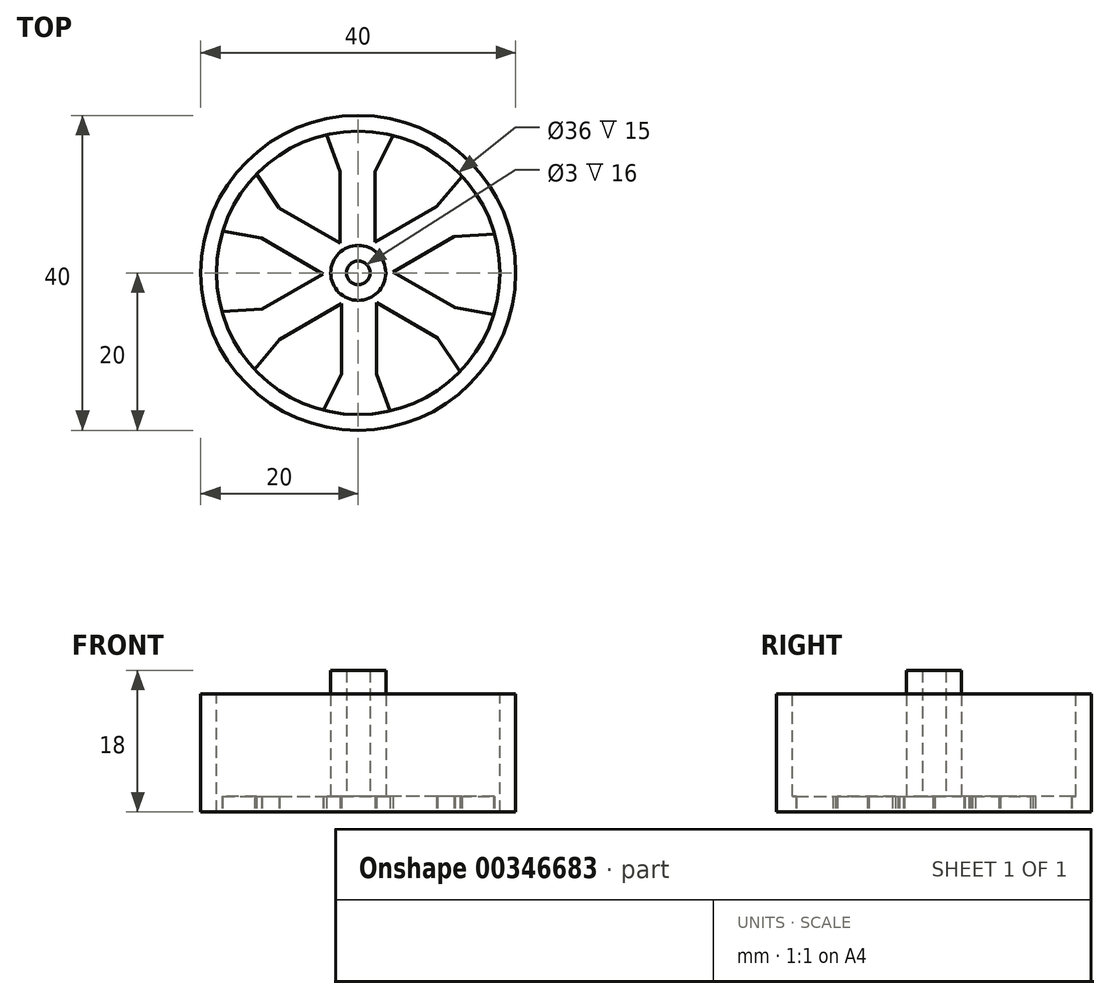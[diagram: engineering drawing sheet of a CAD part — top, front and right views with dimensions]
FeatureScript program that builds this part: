
annotation { "Feature Type Name" : "Feature", "Feature Type Description" : "" }
export const myFeature = defineFeature(function(context is Context, id is Id, definition is map)
    precondition{}
    {
        {
            var Q0;
            Q0=qCreatedBy(makeId("Top.planeOp"),FACE);
            var sketch = newSketch(context, id + "F0", { "sketchPlane" : qUnion([Q0])});
            skCircle(sketch, "E0", {"center": v(0, 0) * mm, "radius": 20 * mm});
            skSolve(sketch);
        }
        {
            var Q0;
            Q0=makeQuery(id+"F0.imprint","IMPRINT",FACE,{"disambiguationData":[TD([[makeQuery(id+"F0.imprint","IMPRINT",EDGE,{"derivedFrom":sQuery(id+"F0.wireOp",EDGE,"E0")}),1.0]])]});
            extrude(context, id + "F1", {"entities" : qUnion([Q0]), "depth" : 15 * mm});
        }
        {
            var Q0;
            Q0=makeQuery(id+"F1.opExtrude","CAP_FACE",FACE,{"disambiguationData":[OSD([sQuery(id+"F0.wireOp",EDGE,"E0")])],"isStart":false});
            var sketch = newSketch(context, id + "F2", { "sketchPlane" : qUnion([Q0])});
            skCircle(sketch, "E1", {"center": v(0, 0) * mm, "radius": 18 * mm});
            skSolve(sketch);
        }
        {
            var Q0;
            Q0=makeQuery(id+"F2.imprint","IMPRINT",FACE,{"disambiguationData":[TD([[makeQuery(id+"F2.imprint","IMPRINT",EDGE,{"derivedFrom":sQuery(id+"F2.wireOp",EDGE,"E1")}),1.0]])]});
            extrude(context, id + "F3", {"entities" : qUnion([Q0]), "operationType" : NewBodyOperationType.REMOVE, "oppositeDirection" : true, "depth" : 13 * mm});
        }
        {
            var Q0;
            Q0=makeQuery(id+"F3.boolean.opBoolean","COPY",FACE,{"derivedFrom":makeQuery(id+"F3.opExtrude","CAP_FACE",FACE,{"disambiguationData":[OSD([sQuery(id+"F2.wireOp",EDGE,"E1")])],"isStart":false})});
            var sketch = newSketch(context, id + "F4", { "sketchPlane" : qUnion([Q0])});
            skCircle(sketch, "E2", {"center": v(0, 0) * mm, "radius": 1.5 * mm});
            skCircle(sketch, "E3", {"center": v(0, 0) * mm, "radius": 3.5 * mm});
            skSolve(sketch);
        }
        {
            var Q0;
            Q0=makeQuery(id+"F4.imprint","IMPRINT",FACE,{"disambiguationData":[TD([[makeQuery(id+"F4.imprint","IMPRINT",EDGE,{"derivedFrom":sQuery(id+"F4.wireOp",EDGE,"E2")}),-1.0]])]});
            extrude(context, id + "F5", {"entities" : qUnion([Q0]), "operationType" : NewBodyOperationType.ADD, "depth" : 16 * mm});
        }
        {
            var Q0;
            Q0=qCreatedBy(makeId("Top.planeOp"),FACE);
            var sketch = newSketch(context, id + "F6", { "sketchPlane" : qUnion([Q0])});
            skCircle(sketch, "E4", {"center": v(0, 0) * mm, "radius": 18 * mm});
            skSolve(sketch);
        }
        {
            var Q0;
            Q0=makeQuery(id+"F6.imprint","IMPRINT",FACE,{"disambiguationData":[TD([[makeQuery(id+"F6.imprint","IMPRINT",EDGE,{"derivedFrom":sQuery(id+"F6.wireOp",EDGE,"E4")}),1.0]])]});
            var sketch = newSketch(context, id + "F7", { "sketchPlane" : qUnion([Q0])});
            skLineSegment(sketch, "E5", {"start": v(-2.12, -0.86) * mm, "end": v(-2.12, -12.86) * mm});
            skLineSegment(sketch, "E6", {"start": v(2.33, -0.86) * mm, "end": v(2.33, -12.86) * mm});
            skLineSegment(sketch, "E7", {"start": v(2.33, -12.86) * mm, "end": v(4.42, -18.61) * mm});
            skLineSegment(sketch, "E8", {"start": v(-2.12, -12.86) * mm, "end": v(-5, -18.61) * mm});
            skLineSegment(sketch, "E9.1.0", {"start": v(-0.32, -2.26) * mm, "end": v(10.08, -8.26) * mm});
            skLineSegment(sketch, "E9.1.1", {"start": v(10.08, -8.26) * mm, "end": v(13.62, -13.63) * mm});
            skLineSegment(sketch, "E9.1.2", {"start": v(12.3, -4.42) * mm, "end": v(18.33, -5.48) * mm});
            skLineSegment(sketch, "E9.1.3", {"start": v(1.9, 1.58) * mm, "end": v(12.3, -4.42) * mm});
            skLineSegment(sketch, "E9.2.0", {"start": v(1.8, -1.4) * mm, "end": v(12.2, 4.6) * mm});
            skLineSegment(sketch, "E9.2.1", {"start": v(12.2, 4.6) * mm, "end": v(18.61, 4.98) * mm});
            skLineSegment(sketch, "E9.2.2", {"start": v(9.97, 8.44) * mm, "end": v(13.9, 13.13) * mm});
            skLineSegment(sketch, "E9.2.3", {"start": v(-0.42, 2.44) * mm, "end": v(9.97, 8.44) * mm});
            skLineSegment(sketch, "E9.3.0", {"start": v(2.12, 0.86) * mm, "end": v(2.12, 12.86) * mm});
            skLineSegment(sketch, "E9.3.1", {"start": v(2.12, 12.86) * mm, "end": v(5, 18.61) * mm});
            skLineSegment(sketch, "E9.3.2", {"start": v(-2.33, 12.86) * mm, "end": v(-4.42, 18.61) * mm});
            skLineSegment(sketch, "E9.3.3", {"start": v(-2.33, 0.86) * mm, "end": v(-2.33, 12.86) * mm});
            skLineSegment(sketch, "E9.4.0", {"start": v(0.32, 2.26) * mm, "end": v(-10.08, 8.26) * mm});
            skLineSegment(sketch, "E9.4.1", {"start": v(-10.08, 8.26) * mm, "end": v(-13.62, 13.63) * mm});
            skLineSegment(sketch, "E9.4.2", {"start": v(-12.3, 4.42) * mm, "end": v(-18.33, 5.48) * mm});
            skLineSegment(sketch, "E9.4.3", {"start": v(-1.9, -1.58) * mm, "end": v(-12.3, 4.42) * mm});
            skLineSegment(sketch, "E9.5.0", {"start": v(-1.8, 1.4) * mm, "end": v(-12.2, -4.6) * mm});
            skLineSegment(sketch, "E9.5.1", {"start": v(-12.2, -4.6) * mm, "end": v(-18.61, -4.98) * mm});
            skLineSegment(sketch, "E9.5.2", {"start": v(-9.97, -8.44) * mm, "end": v(-13.9, -13.13) * mm});
            skLineSegment(sketch, "E9.5.3", {"start": v(0.42, -2.44) * mm, "end": v(-9.97, -8.44) * mm});
            skPoint(sketch, "E9.center", {"position": v(0, 0) * mm});
            skSolve(sketch);
        }
        {
            var Q0;
            {var subQ3=sQuery(id+"F7.wireOp",EDGE,"E6");var subQ5=sQuery(id+"F7.wireOp",EDGE,"E7");var subQ6=makeQuery(id+"F7.imprint","INTERSECT",VERTEX,{"derivedFrom":[subQ3,subQ5]});Q0=makeQuery(id+"F7.imprint","IMPRINT",FACE,{"disambiguationData":[TD([[makeQuery(id+"F7.imprint","IMPRINT",EDGE,{"disambiguationData":[TD([[subQ6,1.0]])],"derivedFrom":subQ3}),1.0]])]});}
            var Q1;
            {var subQ5=sQuery(id+"F7.wireOp",EDGE,"E5");var subQ7=sQuery(id+"F7.wireOp",EDGE,"E8");var subQ8=makeQuery(id+"F7.imprint","INTERSECT",VERTEX,{"derivedFrom":[subQ5,subQ7]});Q1=makeQuery(id+"F7.imprint","IMPRINT",FACE,{"disambiguationData":[TD([[makeQuery(id+"F7.imprint","IMPRINT",EDGE,{"disambiguationData":[TD([[subQ8,1.0]])],"derivedFrom":subQ5}),-1.0]])]});}
            var Q2;
            {var subQ3=sQuery(id+"F7.wireOp",EDGE,"E9.4.3");var subQ5=sQuery(id+"F7.wireOp",EDGE,"E9.4.2");var subQ6=makeQuery(id+"F7.imprint","INTERSECT",VERTEX,{"derivedFrom":[subQ5,subQ3]});Q2=makeQuery(id+"F7.imprint","IMPRINT",FACE,{"disambiguationData":[TD([[makeQuery(id+"F7.imprint","IMPRINT",EDGE,{"disambiguationData":[TD([[subQ6,-1.0]])],"derivedFrom":subQ5}),1.0]])]});}
            var Q3;
            {var subQ3=sQuery(id+"F7.wireOp",EDGE,"E9.3.3");var subQ5=sQuery(id+"F7.wireOp",EDGE,"E9.3.2");var subQ6=makeQuery(id+"F7.imprint","INTERSECT",VERTEX,{"derivedFrom":[subQ5,subQ3]});Q3=makeQuery(id+"F7.imprint","IMPRINT",FACE,{"disambiguationData":[TD([[makeQuery(id+"F7.imprint","IMPRINT",EDGE,{"disambiguationData":[TD([[subQ6,-1.0]])],"derivedFrom":subQ5}),1.0]])]});}
            var Q4;
            {var subQ3=sQuery(id+"F7.wireOp",EDGE,"E9.2.3");var subQ5=sQuery(id+"F7.wireOp",EDGE,"E9.2.2");var subQ6=makeQuery(id+"F7.imprint","INTERSECT",VERTEX,{"derivedFrom":[subQ5,subQ3]});Q4=makeQuery(id+"F7.imprint","IMPRINT",FACE,{"disambiguationData":[TD([[makeQuery(id+"F7.imprint","IMPRINT",EDGE,{"disambiguationData":[TD([[subQ6,-1.0]])],"derivedFrom":subQ5}),1.0]])]});}
            var Q5;
            {var subQ3=sQuery(id+"F7.wireOp",EDGE,"E9.1.3");var subQ5=sQuery(id+"F7.wireOp",EDGE,"E9.1.2");var subQ6=makeQuery(id+"F7.imprint","INTERSECT",VERTEX,{"derivedFrom":[subQ5,subQ3]});Q5=makeQuery(id+"F7.imprint","IMPRINT",FACE,{"disambiguationData":[TD([[makeQuery(id+"F7.imprint","IMPRINT",EDGE,{"disambiguationData":[TD([[subQ6,-1.0]])],"derivedFrom":subQ5}),1.0]])]});}
            extrude(context, id + "F8", {"entities" : qUnion([Q0, Q1, Q2, Q3, Q4, Q5]), "operationType" : NewBodyOperationType.REMOVE, "depth" : 10 * mm});
        }
    });
